# Revit family: Wall family template
name_source: partatom
category: Lighting Fixtures
revit_build: Autodesk Revit 2018 (Build: 20170223_1515(x64)
units: mm (PartAtom-declared; Revit-internal decimal feet)

## family parameters
Always vertical = Yes
Cut with Voids When Loaded = No
Host = Wall
Light Source = No
OmniClass Number = 23.80.70.00
OmniClass Title = Lighting
Part Type = Normal
Room Calculation Point = No
Round Connector Dimension = Use Diameter
Shared = No

## types (2) — shared parameters
Main Material = Metal - Steel
Manufacturer = Astro Lighting Ltd
Manufacturer URL - Europe and Rest of World = www.astrolighting.com
Manufacturer URL - North America = us.astrolighting.com
URL = www.astrolighting.com

## per-type parameters (varying)
| type | ADA compliant | Dimmable | Dimming Method | Driver Included | Driver Required | Efficacy (lm/w) | Electrical Class | Lamp | Length of Cable Supplied | Light Source Fixed | Location / IP Rating | Main Finish | Power (Watts) | Product CCT | Product CRI | Product Dimensions (MM) | Product Location | Product SKU | Product URL | Product Weight (KG) |
| CE | N / A | No | Not Applicable | Not Applicable | Not Applicable | Not Applicable | 1 | E27 | 2500mm | Yes | Indoor/IP20 | Cream | 42W Max | Not Applicable | Not Applicable | 570x125x460 | Wall | 1223021 | https://www.astrolighting.com | 1.225 |
| ETL |  |  |  |  | No |  | 0 |  |  |  | DAMP |  |  | 2700K / 3000K | 80 / 90 |  | Bathroom | 1234001 |  |  |

## geometry (parser evidence)
native form markers: Sweep x2
no freeform markers — native parametric forms only
